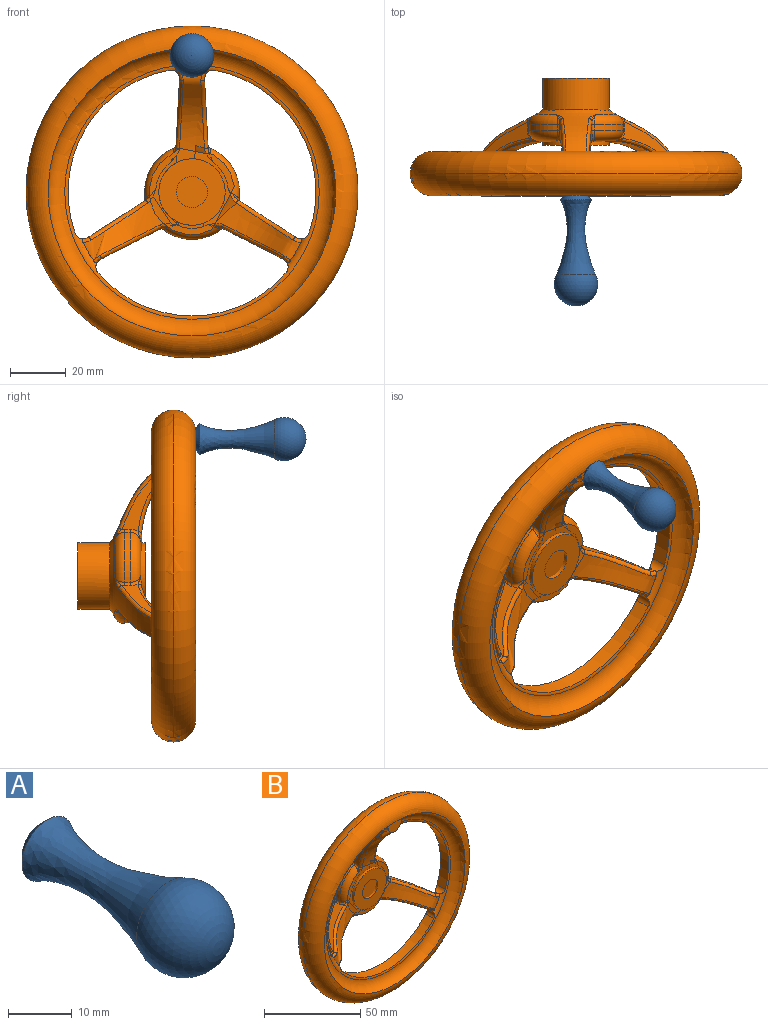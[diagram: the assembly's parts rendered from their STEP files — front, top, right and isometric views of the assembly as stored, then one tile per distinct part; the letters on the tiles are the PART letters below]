
ASSEMBLY  parts=2 mates=1
PART A: 4 faces, bbox 15.6x39.7x15.6 mm
  f0: revolved ~26.72x13.93mm, area 745.5mm2, adj f1,f3
  f1: cone r=5.59mm half-angle=45.7deg, axis (0,-1,0), area 67.3mm2, adj f0,f2
  f2: plane 7.98x7.98mm, normal (0,1,0), area 50mm2, adj f1
  f3: sphere r=7.82mm, area 559.6mm2, adj f0
PART B: 108 faces, bbox 128.9x43.8x128.9 mm
  f0: torus R=45.62mm, axis (0,-1,0), area 403.7mm2, adj f1,f4,f5,f11,f21,f24,f25,f27
  f1: torus R=45.46mm, axis (0,-1,0), area 2423.6mm2, adj f0,f9,f99,f101,f102,f103,f104,f105
  f2: cone r=43.02mm half-angle=3.4deg, axis (0,-1,0), area 3.3mm2, adj f6,f17,f62,f80
  f3: cone r=43.02mm half-angle=3.4deg, axis (0,-1,0), area 3.3mm2, adj f6,f17,f18,f71,f89
  f4: cone r=43.02mm half-angle=3.4deg, axis (0,-1,0), area 0.6mm2, adj f0,f19,f54,f72
  f5: cone r=43.02mm half-angle=3.4deg, axis (0,-1,0), area 0.6mm2, adj f0,f19,f20,f63,f81
  f6: torus R=45.62mm, axis (0,-1,0), area 381.8mm2, adj f2,f3,f7,f10,f21,f24,f25,f27
  f7: torus R=45.46mm, axis (0,-1,0), area 2572.6mm2, adj f6,f8
  f8: torus R=51.6mm, axis (0,-1,0), area 4434.4mm2, adj f7,f9
  f9: torus R=51.6mm, axis (0,-1,0), area 4428.6mm2, adj f1,f8
  f10: cone r=43.02mm half-angle=3.4deg, axis (0,-1,0), area 3.3mm2, adj f6,f17,f53,f98
  f11: cone r=43.02mm half-angle=3.4deg, axis (0,-1,0), area 0.6mm2, adj f0,f19,f45,f90
  f12: cylinder r=11.9mm len=23.8mm, axis (0,1,0), area 119.8mm2, adj f15,f19
  f13: cylinder r=5.58mm len=24.13mm, axis (0,1,0), area 845.3mm2, adj f15,f16
  f14: cylinder r=11.9mm len=23.8mm, axis (0,1,0), area 857.3mm2, adj f16,f17
  f15: plane 23.8x23.8mm, normal (0,-1,0), area 347.2mm2, adj f12,f13
  f16: plane 23.8x23.8mm, normal (0,1,0), area 347.2mm2, adj f13,f14
  f17: revolved ~85.33x85.33mm, area 7527.4mm2, adj f2,f3,f10,f14,f18,f39,f40,f41
  f18: revolved ~1.27x0.39mm, area 0.1mm2, adj f3,f17,f71
  f19: revolved ~85.77x85.77mm, area 6310.8mm2, adj f4,f5,f11,f12,f20,f42,f43,f44
  f20: revolved ~1.53x0.53mm, area 0.3mm2, adj f5,f19,f63
  f21: cylinder r=44.45mm len=58.41mm, axis (0,1,0), area 452.1mm2, adj f0,f6,f24,f25
  f22: cylinder r=17.02mm len=17.95mm, axis (0,1,0), area 46.3mm2, adj f41,f44,f85,f94
  f23: plane 24.57x18.88mm, normal (-1,0,0.05), area 93.6mm2, adj f24,f82,f84,f85,f86,f88
  f24: cylinder r=3.14mm len=5.9mm, axis (0,1,0), area 20.8mm2, adj f0,f6,f21,f23,f81,f89
  f25: cylinder r=3.14mm len=5.9mm, axis (0,1,0), area 20.8mm2, adj f0,f6,f21,f26,f90,f98
  f26: plane 20.65x18.88mm, normal (-0.54,0,0.84), area 93.6mm2, adj f25,f91,f93,f94,f95,f97
  f27: cylinder r=44.45mm len=58.41mm, axis (0,1,0), area 452.1mm2, adj f0,f6,f31,f32
  f28: plane 24.57x18.88mm, normal (1,0,0.05), area 93.6mm2, adj f32,f64,f66,f67,f68,f70
  f29: cylinder r=17.02mm len=17.95mm, axis (0,1,0), area 46.3mm2, adj f40,f43,f67,f76
  f30: plane 20.65x18.88mm, normal (0.54,0,0.84), area 93.6mm2, adj f31,f73,f75,f76,f77,f79
  f31: cylinder r=3.14mm len=5.9mm, axis (0,1,0), area 20.8mm2, adj f0,f6,f27,f30,f72,f80
  f32: cylinder r=3.14mm len=5.9mm, axis (0,1,0), area 20.8mm2, adj f0,f6,f27,f28,f63,f71
  f33: cylinder r=44.45mm len=67.45mm, axis (0,1,0), area 452.1mm2, adj f0,f6,f36,f37
  f34: cylinder r=17.02mm len=20.72mm, axis (0,1,0), area 46.3mm2, adj f39,f42,f49,f58
  f35: plane 21.92x18.88mm, normal (0.45,0,-0.89), area 93.6mm2, adj f36,f46,f48,f49,f50,f52
  f36: cylinder r=3.14mm len=5.9mm, axis (0,1,0), area 20.8mm2, adj f0,f6,f33,f35,f45,f53
  f37: cylinder r=3.14mm len=5.9mm, axis (0,1,0), area 20.8mm2, adj f0,f6,f33,f38,f54,f62
  f38: plane 21.92x18.88mm, normal (-0.45,0,-0.89), area 93.6mm2, adj f37,f55,f57,f58,f59,f61
  f39: torus R=13.21mm, axis (0,1,0), area 84.6mm2, adj f17,f34,f50,f59
  f40: torus R=13.21mm, axis (0,1,0), area 84.6mm2, adj f17,f29,f68,f77
  f41: torus R=13.21mm, axis (0,1,0), area 84.6mm2, adj f17,f22,f86,f95
  f42: torus R=13.21mm, axis (0,1,0), area 106.6mm2, adj f19,f34,f48,f57
  f43: torus R=13.21mm, axis (0,1,0), area 106.6mm2, adj f19,f29,f66,f75
  f44: torus R=13.21mm, axis (0,1,0), area 106.6mm2, adj f19,f22,f84,f93
  f45: bspline ~3.3x3.02mm, area 5.1mm2, adj f0,f11,f19,f36,f46
  f46: bspline ~24.7x14.69mm, area 59.3mm2, adj f19,f35,f45,f47
  f47: bspline ~6.23x1.9mm, area 3.5mm2, adj f19,f46,f48
  f48: bspline ~6.55x5.38mm, area 7.9mm2, adj f35,f42,f47,f49
  f49: cylinder r=1.27mm len=2.08mm, axis (0,1,0), area 3mm2, adj f34,f35,f48,f50
  f50: bspline ~5.18x4.45mm, area 3.3mm2, adj f35,f39,f49,f51
  f51: bspline ~5.26x2.85mm, area 2.8mm2, adj f17,f50,f52
  f52: bspline ~23.08x19.45mm, area 56.7mm2, adj f17,f35,f51,f53
  f53: bspline ~2.84x2.38mm, area 3.6mm2, adj f6,f10,f17,f36,f52
  f54: bspline ~3.5x3.36mm, area 5.1mm2, adj f0,f4,f19,f37,f55
  f55: bspline ~24.7x14.69mm, area 59.3mm2, adj f19,f38,f54,f56
  f56: bspline ~6.23x1.9mm, area 3.7mm2, adj f19,f55,f57
  f57: bspline ~6.55x5.38mm, area 7.9mm2, adj f38,f42,f56,f58
  f58: cylinder r=1.27mm len=2.08mm, axis (0,1,0), area 3mm2, adj f34,f38,f57,f59
  f59: bspline ~5.18x4.45mm, area 3.3mm2, adj f38,f39,f58,f60
  f60: bspline ~5.26x2.85mm, area 2.8mm2, adj f17,f59,f61
  f61: bspline ~23.08x19.45mm, area 56.7mm2, adj f17,f38,f60,f62
  f62: bspline ~2.84x2.38mm, area 3.6mm2, adj f2,f6,f17,f37,f61
  f63: bspline ~3.98x2.08mm, area 5.1mm2, adj f0,f5,f19,f20,f32,f64
  f64: bspline ~27.34x14.69mm, area 59.3mm2, adj f19,f28,f63,f65
  f65: bspline ~5.11x2.88mm, area 3.7mm2, adj f19,f64,f66
  f66: bspline ~6.77x5.38mm, area 7.9mm2, adj f28,f43,f65,f67
  f67: cylinder r=1.27mm len=2.08mm, axis (0,1,0), area 3mm2, adj f28,f29,f66,f68
  f68: bspline ~5.18x4.4mm, area 3.3mm2, adj f28,f40,f67,f69
  f69: bspline ~4.77x2.85mm, area 2.8mm2, adj f17,f68,f70
  f70: bspline ~25.24x19.45mm, area 56.7mm2, adj f17,f28,f69,f71
  f71: bspline ~3.04x1.89mm, area 3.6mm2, adj f3,f6,f17,f18,f32,f70
  f72: bspline ~3.49x2.26mm, area 5.1mm2, adj f0,f4,f19,f31,f73
  f73: bspline ~23.62x15.82mm, area 59.3mm2, adj f19,f30,f72,f74
  f74: bspline ~5.24x4.01mm, area 3.5mm2, adj f19,f73,f75
  f75: bspline ~5.69x5.38mm, area 7.9mm2, adj f30,f43,f74,f76
  f76: cylinder r=1.27mm len=2.08mm, axis (0,1,0), area 3mm2, adj f29,f30,f75,f77
  f77: bspline ~5.18x3.7mm, area 3.3mm2, adj f30,f40,f76,f78
  f78: bspline ~4.34x3.38mm, area 2.8mm2, adj f17,f77,f79
  f79: bspline ~21.4x19.45mm, area 56.7mm2, adj f17,f30,f78,f80
  f80: bspline ~2.43x1.91mm, area 3.6mm2, adj f2,f6,f17,f31,f79
  f81: bspline ~3.57x1.85mm, area 5.1mm2, adj f0,f5,f19,f24,f82
  f82: bspline ~27.34x14.69mm, area 59.3mm2, adj f19,f23,f81,f83
  f83: bspline ~5.11x2.88mm, area 3.5mm2, adj f19,f82,f84
  f84: bspline ~6.77x5.38mm, area 7.9mm2, adj f23,f44,f83,f85
  f85: cylinder r=1.27mm len=2.08mm, axis (0,1,0), area 3mm2, adj f22,f23,f84,f86
  f86: bspline ~5.18x4.4mm, area 3.3mm2, adj f23,f41,f85,f87
  f87: bspline ~4.77x2.85mm, area 2.8mm2, adj f17,f86,f88
  f88: bspline ~25.22x19.38mm, area 56.7mm2, adj f17,f23,f87,f89
  f89: bspline ~3.04x1.89mm, area 3.6mm2, adj f3,f6,f17,f24,f88
  f90: bspline ~4x2.27mm, area 5.1mm2, adj f0,f11,f19,f25,f91
  f91: bspline ~23.62x15.82mm, area 59.3mm2, adj f19,f26,f90,f92
  f92: bspline ~5.24x4.01mm, area 3.7mm2, adj f19,f91,f93
  f93: bspline ~5.69x5.38mm, area 7.9mm2, adj f26,f44,f92,f94
  f94: cylinder r=1.27mm len=2.08mm, axis (0,1,0), area 3mm2, adj f22,f26,f93,f95
  f95: bspline ~5.18x3.7mm, area 3.3mm2, adj f26,f41,f94,f96
  f96: bspline ~4.34x3.38mm, area 2.8mm2, adj f17,f95,f97
  f97: bspline ~21.4x19.45mm, area 56.7mm2, adj f17,f26,f96,f98
  f98: bspline ~2.43x1.91mm, area 3.5mm2, adj f6,f10,f17,f25,f97
  f99: plane 14.32x6.05mm, normal (0,-1,0), area 50.8mm2, adj f1,f100,f101,f102,f103,f104
  f100: cone r=4.95mm half-angle=15deg, axis (0,1,0), area 50.4mm2, adj f99,f101,f104,f105,f106,f107
  f101: cone r=2.15mm half-angle=15deg, axis (0,-1,0), area 4.2mm2, adj f1,f99,f100,f102,f106
  f102: plane 0.62x0.27mm, normal (0.68,0,0.73), area 0mm2, adj f1,f99,f101
  f103: plane 0.68x0.32mm, normal (-0.67,0,0.74), area 0mm2, adj f1,f99,f104
  f104: cone r=2.15mm half-angle=15deg, axis (0,-1,0), area 4.3mm2, adj f1,f99,f100,f103,f105
  f105: bspline ~6x4.29mm, area 8.8mm2, adj f1,f100,f104,f107
  f106: bspline ~6.04x3.89mm, area 8.8mm2, adj f1,f100,f101,f107
  f107: bspline ~11.18x2.98mm, area 12.1mm2, adj f0,f1,f100,f105,f106
PLACE A t=(-21,43.49,12.17)mm
PLACE B t=(-21,19.89,10.4)mm
MATE fastened A.f1 <-> B.f99  axis (0,1,0) through (-21,12.02,59.42)mm
